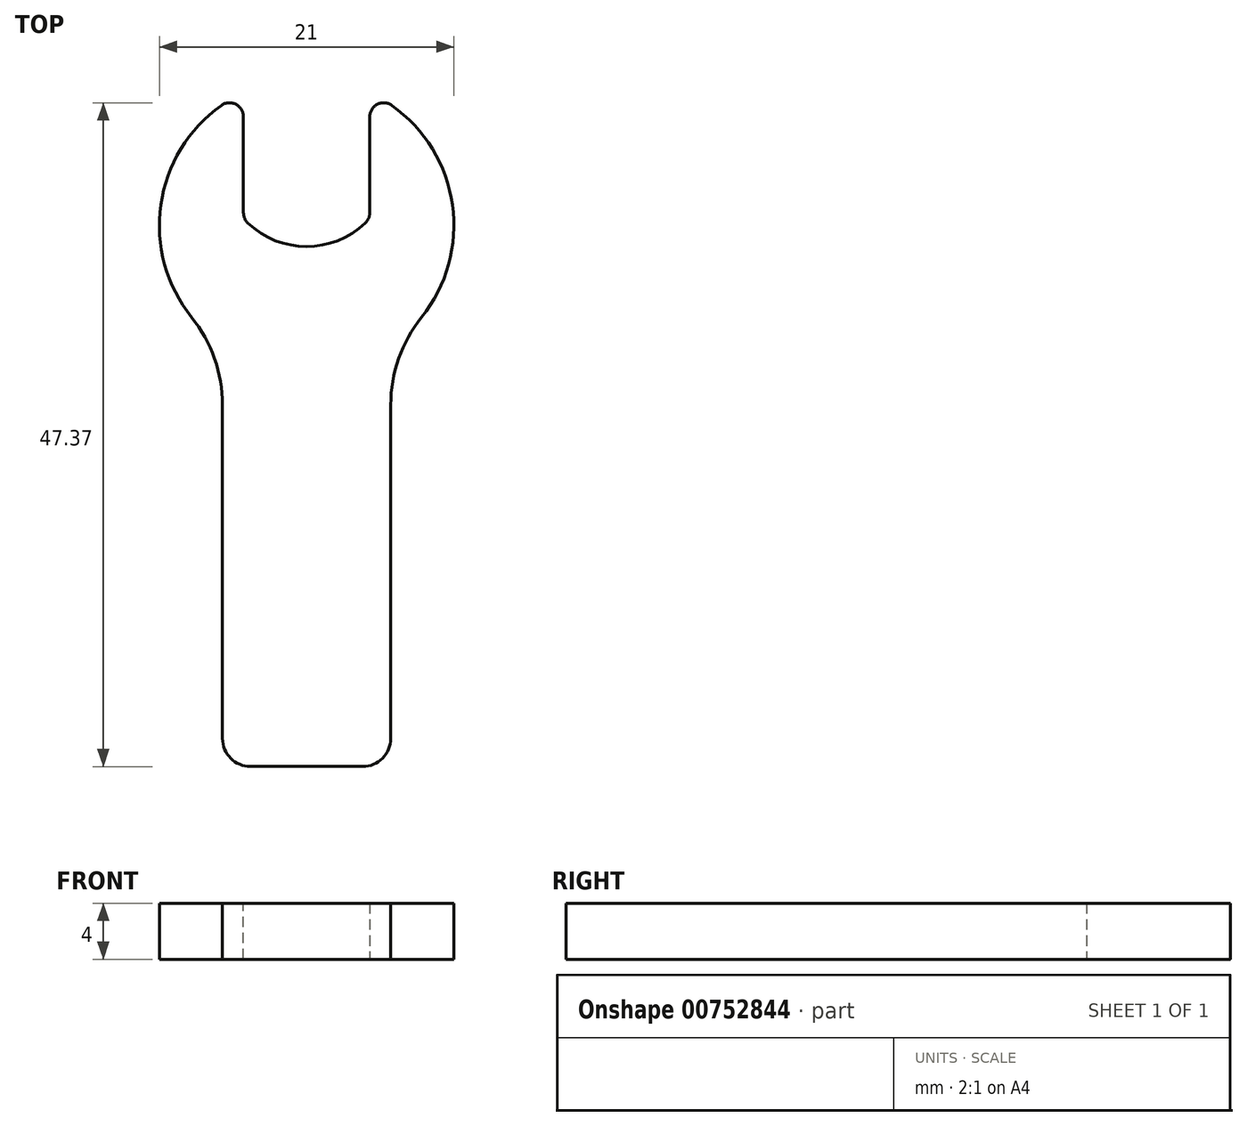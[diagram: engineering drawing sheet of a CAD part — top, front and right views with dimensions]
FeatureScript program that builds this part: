
annotation { "Feature Type Name" : "Feature", "Feature Type Description" : "" }
export const myFeature = defineFeature(function(context is Context, id is Id, definition is map)
    precondition{}
    {
        {
            var Q0;
            Q0=qCreatedBy(makeId("Top.planeOp"),FACE);
            var sketch = newSketch(context, id + "F0", { "sketchPlane" : qUnion([Q0])});
            skArc(sketch, "E0", {"start": v(-4.5, 9.49) * mm, "mid": v(0, -10.5) * mm, "end": v(4.5, 9.49) * mm});
            skLineSegment(sketch, "E1.bottom", {"start": v(6, -8.62) * mm, "end": v(-6, -8.62) * mm});
            skLineSegment(sketch, "E1.top", {"start": v(6, -38.62) * mm, "end": v(-6, -38.62) * mm});
            skLineSegment(sketch, "E1.left", {"start": v(6, -8.62) * mm, "end": v(6, -38.62) * mm});
            skLineSegment(sketch, "E1.right", {"start": v(-6, -8.62) * mm, "end": v(-6, -38.62) * mm});
            skPoint(sketch, "E1.middle", {"position": v(0, -23.62) * mm});
            skLineSegment(sketch, "E2.bottom", {"start": v(-4.5, 9.49) * mm, "end": v(4.5, 9.49) * mm, "construction": true});
            skLineSegment(sketch, "E2.top", {"start": v(-4.5, 0.49) * mm, "end": v(4.5, 0.49) * mm, "construction": true});
            skLineSegment(sketch, "E2.left", {"start": v(-4.5, 9.49) * mm, "end": v(-4.5, 0.49) * mm});
            skLineSegment(sketch, "E2.right", {"start": v(4.5, 9.49) * mm, "end": v(4.5, 0.49) * mm});
            skPoint(sketch, "E2.middle", {"position": v(0, 4.99) * mm});
            skArc(sketch, "E3", {"start": v(-4.5, 0.49) * mm, "mid": v(0, -1.51) * mm, "end": v(4.5, 0.49) * mm});
            skSolve(sketch);
        }
        {
            var Q0;
            {var subQ0=sQuery(id+"F0.wireOp",EDGE,"E1.bottom");Q0=makeQuery(id+"F0.imprint","IMPRINT",FACE,{"disambiguationData":[TD([[makeQuery(id+"F0.imprint","IMPRINT",EDGE,{"derivedFrom":subQ0}),-1.0]])]});}
            var Q1;
            Q1 = qSketchRegion(id + "F0", true);
            extrude(context, id + "F1", {"entities" : qUnion([Q0, Q1]), "depth" : 4 * mm, "offsetDistance" : 25 * mm});
        }
        {
            var Q0;
            Q0=makeQuery(id+"F1.opExtrude","SWEPT_EDGE",EDGE,{"disambiguationData":[OSD([sQuery(id+"F0.wireOp",EDGE,"E0"),sQuery(id+"F0.wireOp",EDGE,"E1.bottom"),sQuery(id+"F0.wireOp",EDGE,"E1.right")])]});
            var Q1;
            Q1=makeQuery(id+"F1.opExtrude","SWEPT_EDGE",EDGE,{"disambiguationData":[OSD([sQuery(id+"F0.wireOp",EDGE,"E0"),sQuery(id+"F0.wireOp",EDGE,"E1.bottom"),sQuery(id+"F0.wireOp",EDGE,"E1.left")])]});
            fillet(context, id + "F2", {"entities" : qUnion([Q0, Q1]), "radius" : 10 * mm, "tangentPropagation" : true, "allowEdgeOverflow" : false});
        }
        {
            var Q0;
            Q0=makeQuery(id+"F1.opExtrude","SWEPT_EDGE",EDGE,{"disambiguationData":[OSD([sQuery(id+"F0.wireOp",EDGE,"E0"),sQuery(id+"F0.wireOp",EDGE,"E2.left")])]});
            var Q1;
            Q1=makeQuery(id+"F1.opExtrude","SWEPT_EDGE",EDGE,{"disambiguationData":[OSD([sQuery(id+"F0.wireOp",EDGE,"E0"),sQuery(id+"F0.wireOp",EDGE,"E2.right")])]});
            fillet(context, id + "F3", {"entities" : qUnion([Q0, Q1]), "radius" : 1 * mm, "tangentPropagation" : true, "allowEdgeOverflow" : false});
        }
        {
            var Q0;
            Q0=makeQuery(id+"F1.opExtrude","SWEPT_EDGE",EDGE,{"disambiguationData":[OSD([sQuery(id+"F0.wireOp",EDGE,"E1.top"),sQuery(id+"F0.wireOp",EDGE,"E1.left")])]});
            var Q1;
            Q1=makeQuery(id+"F1.opExtrude","SWEPT_EDGE",EDGE,{"disambiguationData":[OSD([sQuery(id+"F0.wireOp",EDGE,"E1.top"),sQuery(id+"F0.wireOp",EDGE,"E1.right")])]});
            fillet(context, id + "F4", {"entities" : qUnion([Q0, Q1]), "radius" : 2 * mm, "tangentPropagation" : true, "allowEdgeOverflow" : false});
        }
        {
            var Q0;
            Q0=makeQuery(id+"F1.opExtrude","SWEPT_EDGE",EDGE,{"disambiguationData":[OSD([sQuery(id+"F0.wireOp",EDGE,"E2.right"),sQuery(id+"F0.wireOp",EDGE,"E3")])]});
            var Q1;
            Q1=makeQuery(id+"F1.opExtrude","SWEPT_EDGE",EDGE,{"disambiguationData":[OSD([sQuery(id+"F0.wireOp",EDGE,"E2.left"),sQuery(id+"F0.wireOp",EDGE,"E3")])]});
            fillet(context, id + "F5", {"entities" : qUnion([Q0, Q1]), "radius" : 1 * mm, "tangentPropagation" : true, "allowEdgeOverflow" : false});
        }
    });
